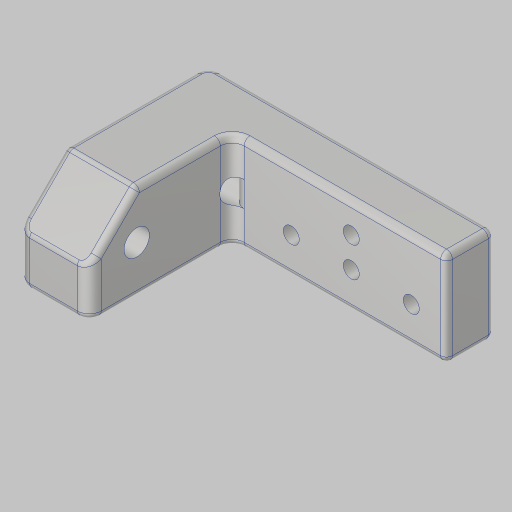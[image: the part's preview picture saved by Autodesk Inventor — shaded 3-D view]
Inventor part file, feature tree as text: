
AUTODESK INVENTOR PART (.ipt)
format: ipt  version: 2023.5 (Build 275446000, 446)  size: 254,976 bytes
history: native  units: in
note: dims shown in document units (in); Inventor stores cm internally (conversion verified against a paired STEP export)
features: sketch x5, fillet x4, extrude x3, projected_geometry x3, hole x2, plane x2
ambient origin geometry x8: Origin, YZ Plane, XZ Plane, XY Plane, X Axis, Y Axis, Z Axis, Center Point
bodies: Solid1 (feature_tree)
feature tree (19):
  sketch  "Sketch1"  dims[d0=0.6299in d1=0.6299in]
  extrude  "Extrusion1"  Depth=0.6299in
  hole  "Hole2"  [1 undecoded]
  plane  "Work Plane2"
  extrude  "Extrusion2"  Depth=2.0in TaperAngle=0.0deg
  hole  "Hole3"  [1 undecoded]
  fillet  "Fillet1"  Radius=0.375in
  fillet  "Fillet3"  Radius=0.5in
  fillet  "Fillet4"  Radius=0.75in
  extrude  "Extrusion3"  TaperAngle=0.0deg  [1 undecoded]
  fillet  "Fillet5"  Radius=0.125in
  sketch  "Sketch2"  dims[d4=0.625in d6=3.0in]
  plane  "Work Plane1"
  sketch  "Sketch3"  dims[d8=1.0in d9=2.0in d10=0.0in]
  projected_geometry  "Projected Loop1"
  sketch  "Sketch4"  dims[d18=1.005in]
  sketch  "Sketch5"  dims[d19=0.2657in d20=0.38in d21=0.375in d22=0.25in d23=0.5635in d24=0.75in d25=0.0in d26=2.7525in d27=-2.2047in d28=0.375in d29=0.5in d30=0.75in d31=0.0in d32=0.0in d33=0.1673in d34=0.236in d35=0.375in d36=0.25in d37=0.5635in d38=0.346in d39=0.0in d40=0.125in d42=0.125in d44=2.0in d45=0.375in d46=0.315in d47=0.0625in d48=45.0deg d49=0.5in d50=0.0in d51=0.0in d52=0.0625in]
  projected_geometry  "Projected Loop2"
  projected_geometry  "Projected Loop3"
note: 3 required parameter values undecoded (feature->parameter linkage not recoverable at this tier; creation-order binding heuristic only, values carry confidence <= 0.55)
